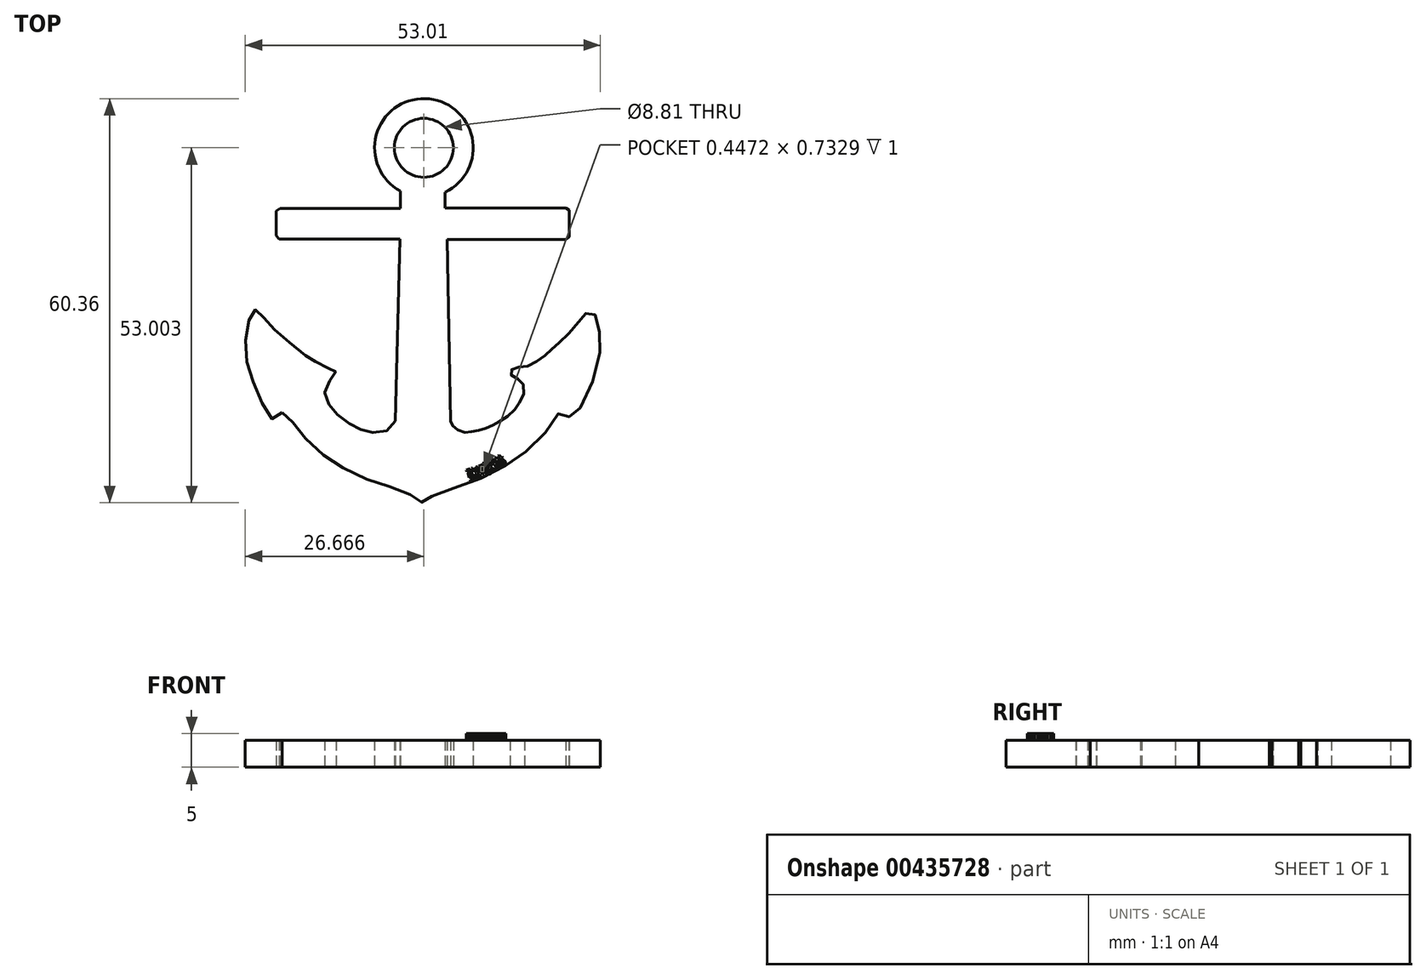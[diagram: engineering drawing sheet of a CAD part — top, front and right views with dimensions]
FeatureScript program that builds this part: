
annotation { "Feature Type Name" : "Feature", "Feature Type Description" : "" }
export const myFeature = defineFeature(function(context is Context, id is Id, definition is map)
    precondition{}
    {
        {
            var Q0;
            Q0=qCreatedBy(makeId("Top.planeOp"),FACE);
            var sketch = newSketch(context, id + "F0", { "sketchPlane" : qUnion([Q0])});
            skLineSegment(sketch, "E0", {"start": v(-3.3, 13.86) * mm, "end": v(-3.3, 11.3) * mm});
            skLineSegment(sketch, "E1", {"start": v(-3.3, 11.3) * mm, "end": v(-21.24, 11.3) * mm});
            skLineSegment(sketch, "E2", {"start": v(-21.8, 10.89) * mm, "end": v(-21.8, 7.19) * mm});
            skLineSegment(sketch, "E3", {"start": v(-21.38, 6.66) * mm, "end": v(-3.36, 6.66) * mm});
            skLineSegment(sketch, "E4", {"start": v(-3.36, 6.66) * mm, "end": v(-4.07, -20.48) * mm});
            skLineSegment(sketch, "E5", {"start": v(3.42, 13.68) * mm, "end": v(3.42, 11.35) * mm});
            skLineSegment(sketch, "E6", {"start": v(3.42, 11.35) * mm, "end": v(21.44, 11.35) * mm});
            skLineSegment(sketch, "E7", {"start": v(21.91, 11.01) * mm, "end": v(21.91, 7.03) * mm});
            skLineSegment(sketch, "E8", {"start": v(21.45, 6.62) * mm, "end": v(3.7, 6.62) * mm});
            skLineSegment(sketch, "E9", {"start": v(3.7, 6.62) * mm, "end": v(4.24, -20.49) * mm});
            skArc(sketch, "E10", {"start": v(3.42, 13.68) * mm, "mid": v(0.43, 27.67) * mm, "end": v(-3.3, 13.86) * mm});
            skCircle(sketch, "E11", {"center": v(0.24, 20.31) * mm, "radius": 4.4 * mm});
            skFitSpline(sketch, "E12", {"points": [v(-4.07, -20.48) * mm, v(-5.23, -21.92) * mm, v(-7.33, -22.22) * mm, v(-9.03, -21.84) * mm, v(-10.65, -21.04) * mm, v(-12.64, -19.57) * mm, v(-13.86, -18.1) * mm, v(-14.53, -16.57) * mm, v(-14.1, -14.79) * mm, v(-12.85, -13.53) * mm, v(-13.4, -12.64) * mm, v(-14.07, -12.62) * mm, v(-16.17, -11.5) * mm, v(-17.32, -10.77) * mm, v(-20.98, -7.77) * mm, v(-23.18, -5.64) * mm, v(-24.65, -3.93) * mm, v(-25.17, -4.03) * mm, v(-26.22, -6.79) * mm, v(-26.15, -11.82) * mm, v(-24.4, -16.64) * mm, v(-22.38, -20.2) * mm, v(-20.91, -19.23) * mm], "startDerivative": vector(-22.58, -39.92) * mm, "endDerivative": vector(38.05, 35.16) * mm});
            skFitSpline(sketch, "E13", {"points": [v(-20.91, -19.23) * mm, v(-20.4, -19.23) * mm, v(-19.5, -20.37) * mm, v(-18.92, -21.35) * mm, v(-17.3, -23.24) * mm, v(-15.23, -25.17) * mm, v(-13.73, -26.33) * mm, v(-10.94, -27.99) * mm, v(-8.16, -29.23) * mm, v(-5.67, -30.06) * mm, v(-3.6, -30.73) * mm, v(-1.62, -31.58) * mm, v(-0.68, -32.02) * mm, v(-0.22, -32.58) * mm, v(0.51, -32.63) * mm, v(0.82, -32.27) * mm, v(1.56, -31.6) * mm, v(3.5, -30.9) * mm, v(7.24, -29.65) * mm, v(10.22, -28.4) * mm, v(13.3, -26.59) * mm, v(15.45, -25.03) * mm, v(17.88, -22.78) * mm, v(19.78, -20.34) * mm, v(20.48, -19.23) * mm, v(21, -19.23) * mm, v(21.68, -19.63) * mm, v(22.27, -20.08) * mm, v(23.11, -19.23) * mm, v(24.43, -16.97) * mm, v(26.1, -12.43) * mm, v(26.56, -9.56) * mm, v(26.52, -7.78) * mm, v(26.21, -5.94) * mm, v(25.86, -4.7) * mm, v(25.35, -4.02) * mm, v(24.89, -3.9) * mm, v(24.09, -4.86) * mm, v(21.9, -7.43) * mm], "startDerivative": vector(35.42, 8.92) * mm, "endDerivative": vector(-54.6, -66.3) * mm});
            skFitSpline(sketch, "E14", {"points": [v(21.9, -7.43) * mm, v(19.73, -9.45) * mm, v(18.41, -10.58) * mm, v(16.63, -11.85) * mm, v(14.98, -12.46) * mm, v(13.72, -12.5) * mm, v(13.11, -13.36) * mm, v(13.73, -13.92) * mm, v(14.75, -14.53) * mm, v(15.27, -16.03) * mm, v(14.41, -17.92) * mm, v(13.69, -18.94) * mm, v(12.03, -20.24) * mm, v(10.86, -20.9) * mm, v(9.84, -21.42) * mm, v(8.78, -21.78) * mm, v(7.7, -22) * mm, v(6.8, -22.18) * mm, v(5.78, -22.07) * mm, v(4.76, -21.5) * mm, v(4.4, -20.97) * mm, v(4.24, -20.49) * mm], "startDerivative": vector(-43.3, -41.33) * mm, "endDerivative": vector(-4.47, 16.17) * mm});
            skFitSpline(sketch, "E15", {"points": [v(21.44, 11.35) * mm, v(21.91, 11.01) * mm], "startDerivative": vector(0.47, -0.34) * mm, "endDerivative": vector(0.47, -0.34) * mm});
            skFitSpline(sketch, "E16", {"points": [v(21.91, 7.03) * mm, v(21.45, 6.62) * mm], "startDerivative": vector(-0.46, -0.41) * mm, "endDerivative": vector(-0.46, -0.41) * mm});
            skFitSpline(sketch, "E17", {"points": [v(-21.8, 7.19) * mm, v(-21.38, 6.66) * mm], "startDerivative": vector(0.42, -0.52) * mm, "endDerivative": vector(0.42, -0.52) * mm});
            skFitSpline(sketch, "E18", {"points": [v(-21.24, 11.3) * mm, v(-21.8, 10.89) * mm], "startDerivative": vector(-0.56, -0.4) * mm, "endDerivative": vector(-0.56, -0.4) * mm});
            skSolve(sketch);
        }
        {
            var Q0;
            Q0=makeQuery(id+"F0.imprint","IMPRINT",FACE,{"disambiguationData":[TD([[makeQuery(id+"F0.imprint","IMPRINT",EDGE,{"derivedFrom":sQuery(id+"F0.wireOp",EDGE,"E0")}),1.0]])]});
            extrude(context, id + "F1", {"entities" : qUnion([Q0]), "depth" : 4 * mm});
        }
        {
            var Q0;
            Q0=qCreatedBy(makeId("Top.planeOp"),FACE);
            var sketch = newSketch(context, id + "F2", { "sketchPlane" : qUnion([Q0])});
            skText(sketch, "E19", { "text": "张", "fontName": "NotoSansCJKtc-Bold.otf"});
            const initialGuessF2  = {"E19": [0.007, -0.02945, 0.9397, 0.34202, 0.00147]};
            skSetInitialGuess(sketch, initialGuessF2);
            skSolve(sketch);
        }
        {
            var Q0;
            Q0=qCreatedBy(makeId("Top.planeOp"),FACE);
            var sketch = newSketch(context, id + "F3", { "sketchPlane" : qUnion([Q0])});
            skText(sketch, "E20", { "text": "咏", "fontName": "NotoSansCJKsc-Bold.otf"});
            const initialGuessF3  = {"E20": [0.00896, -0.02873, 0.9067, 0.4218, 0.00156]};
            skSetInitialGuess(sketch, initialGuessF3);
            skSolve(sketch);
        }
        {
            var Q0;
            Q0=qCreatedBy(makeId("Top.planeOp"),FACE);
            var sketch = newSketch(context, id + "F4", { "sketchPlane" : qUnion([Q0])});
            skText(sketch, "E21", { "text": "琳", "fontName": "NotoSansCJKtc-Bold.otf"});
            const initialGuessF4  = {"E21": [0.01099, -0.02778, 0.84516, 0.5345, 0.00139]};
            skSetInitialGuess(sketch, initialGuessF4);
            skSolve(sketch);
        }
        {
            var Q0;
            Q0=makeQuery(id+"F0.imprint","IMPRINT",FACE,{"disambiguationData":[TD([[makeQuery(id+"F0.imprint","IMPRINT",EDGE,{"derivedFrom":sQuery(id+"F0.wireOp",EDGE,"E0")}),1.0]])]});
            extrude(context, id + "F5", {"entities" : qUnion([Q0]), "depth" : 4 * mm});
        }
        {
            var Q0;
            Q0 = qSketchRegion(id + "F3", true);
            var Q1;
            Q1 = qSketchRegion(id + "F4", true);
            var Q2;
            Q2 = qSketchRegion(id + "F2", true);
            extrude(context, id + "F6", {"entities" : qUnion([Q0, Q1, Q2]), "operationType" : NewBodyOperationType.ADD, "depth" : 5 * mm});
        }
    });
